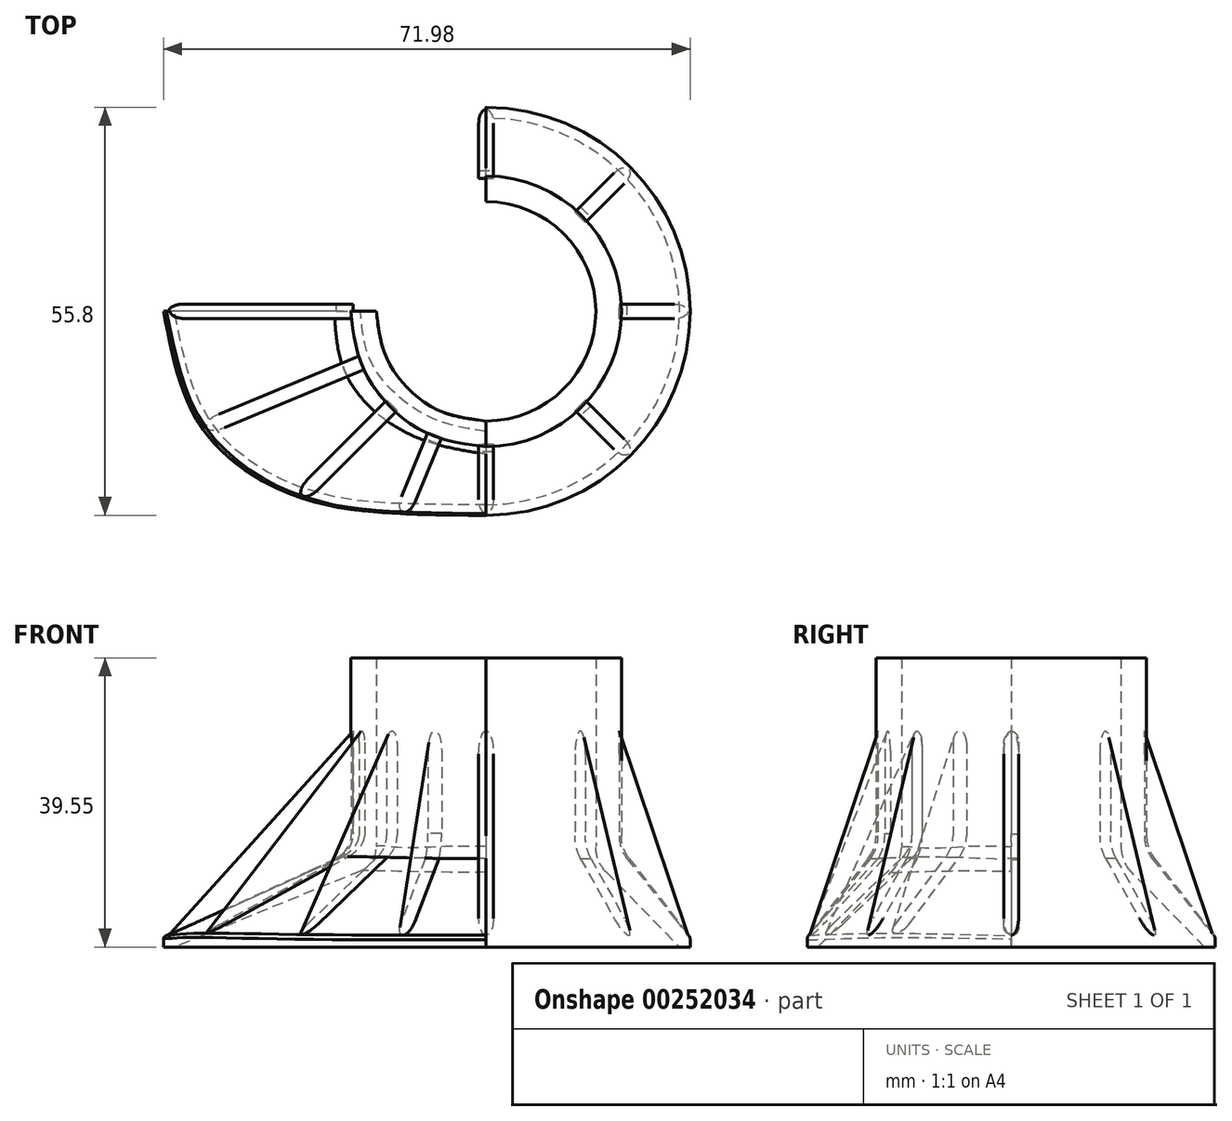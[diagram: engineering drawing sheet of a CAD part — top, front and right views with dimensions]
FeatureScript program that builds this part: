
annotation { "Feature Type Name" : "Feature", "Feature Type Description" : "" }
export const myFeature = defineFeature(function(context is Context, id is Id, definition is map)
    precondition{}
    {
        {
            var Q0;
            Q0=qCreatedBy(makeId("Front.planeOp"),FACE);
            var sketch = newSketch(context, id + "F0", { "sketchPlane" : qUnion([Q0])});
            skLineSegment(sketch, "E0.1", {"start": v(15, 34.55) * mm, "end": v(18.5, 34.55) * mm});
            skLineSegment(sketch, "E1", {"start": v(0, 0) * mm, "end": v(0, -5) * mm, "construction": true});
            skLineSegment(sketch, "E2", {"start": v(0, -5) * mm, "end": v(-50, -5) * mm, "construction": true});
            skLineSegment(sketch, "E3", {"start": v(0, -5) * mm, "end": v(27.9, -5) * mm, "construction": true});
            skLineSegment(sketch, "E4", {"start": v(0, 0) * mm, "end": v(0, 5) * mm, "construction": true});
            skLineSegment(sketch, "E5", {"start": v(0, 5) * mm, "end": v(-50, 5) * mm, "construction": true});
            skLineSegment(sketch, "E6", {"start": v(0, 5) * mm, "end": v(28.45, 5) * mm, "construction": true});
            skLineSegment(sketch, "E7", {"start": v(27.9, -5) * mm, "end": v(26.45, -5) * mm});
            skLineSegment(sketch, "E8", {"start": v(15, 34.55) * mm, "end": v(15, 8.73) * mm});
            skLineSegment(sketch, "E9", {"start": v(26.45, -5) * mm, "end": v(16.43, 5.23) * mm});
            skPoint(sketch, "E10.visualSharp", {"position": v(15, 6.7) * mm});
            skArc(sketch, "E10.filletArc", {"start": v(15, 8.73) * mm, "mid": v(15.37, 6.84) * mm, "end": v(16.43, 5.23) * mm});
            skLineSegment(sketch, "E11", {"start": v(18.5, 34.55) * mm, "end": v(18.5, 10.2) * mm});
            skLineSegment(sketch, "E12", {"start": v(19.55, 7.13) * mm, "end": v(27.7, -3.39) * mm});
            skLineSegment(sketch, "E13", {"start": v(27.9, -4) * mm, "end": v(27.9, -5) * mm});
            skPoint(sketch, "E14.visualSharp", {"position": v(27.9, -3.66) * mm});
            skArc(sketch, "E14.filletArc", {"start": v(27.9, -4) * mm, "mid": v(27.85, -3.68) * mm, "end": v(27.7, -3.39) * mm});
            skPoint(sketch, "E15.visualSharp", {"position": v(18.5, 8.48) * mm});
            skArc(sketch, "E15.filletArc", {"start": v(18.5, 10.2) * mm, "mid": v(18.77, 8.58) * mm, "end": v(19.55, 7.13) * mm});
            skLineSegment(sketch, "E16", {"start": v(0, 5) * mm, "end": v(0, 75) * mm, "construction": true});
            skLineSegment(sketch, "E17", {"start": v(0, -5) * mm, "end": v(0, -75) * mm, "construction": true});
            skSolve(sketch);
        }
        {
            var Q0;
            Q0=qCreatedBy(makeId("Front.planeOp"),FACE);
            var sketch = newSketch(context, id + "F1", { "sketchPlane" : qUnion([Q0])});
            skLineSegment(sketch, "E18.MirrorCS", {"start": v(-15, 34.55) * mm, "end": v(-15, 8.75) * mm});
            skLineSegment(sketch, "E19.MirrorCS", {"start": v(-15, 34.55) * mm, "end": v(-18.5, 34.55) * mm});
            skLineSegment(sketch, "E20.MirrorCS", {"start": v(-18.5, 34.55) * mm, "end": v(-18.5, 10.45) * mm});
            skLineSegment(sketch, "E21", {"start": v(-27.58, -5) * mm, "end": v(-42.58, -5) * mm, "construction": true});
            skLineSegment(sketch, "E22", {"start": v(-17.18, 5.4) * mm, "end": v(-42.58, -5) * mm});
            skLineSegment(sketch, "E23", {"start": v(-42.58, -5) * mm, "end": v(-44.08, -5) * mm});
            skLineSegment(sketch, "E24", {"start": v(-44.08, -5) * mm, "end": v(-44.08, -3.9) * mm});
            skLineSegment(sketch, "E25", {"start": v(-43.71, -3.44) * mm, "end": v(-20.75, 6.96) * mm});
            skPoint(sketch, "E26.visualSharp", {"position": v(-15, 6.28) * mm});
            skArc(sketch, "E26.filletArc", {"start": v(-17.18, 5.4) * mm, "mid": v(-15.6, 6.75) * mm, "end": v(-15, 8.75) * mm});
            skPoint(sketch, "E27.visualSharp", {"position": v(-18.5, 7.98) * mm});
            skArc(sketch, "E27.filletArc", {"start": v(-20.75, 6.96) * mm, "mid": v(-19.11, 8.38) * mm, "end": v(-18.5, 10.45) * mm});
            skPoint(sketch, "E28.visualSharp", {"position": v(-42.58, -5) * mm});
            skLineSegment(sketch, "E28.filletArc", {"start": v(-42.58, -5) * mm, "end": v(-42.58, -5) * mm});
            skPoint(sketch, "E29.visualSharp", {"position": v(-44.08, -3) * mm});
            skArc(sketch, "E29.filletArc", {"start": v(-43.71, -3.44) * mm, "mid": v(-43.97, -3.6) * mm, "end": v(-44.08, -3.9) * mm});
            skSolve(sketch);
        }
        {
            var Q0;
            Q0=makeQuery(id+"F0.imprint","IMPRINT",FACE,{"disambiguationData":[TD([[makeQuery(id+"F0.imprint","IMPRINT",EDGE,{"derivedFrom":sQuery(id+"F0.wireOp",EDGE,"E0.1")}),-1.0]])]});
            var Q1;
            Q1=sQuery(id+"F0.wireOp",EDGE,"E4");
            revolve(context, id + "F2", {"entities" : qUnion([Q0]), "axis" : qUnion([Q1]), "revolveType" : RevolveType.SYMMETRIC, "angle" : 180 * degree});
        }
        {
            var Q0;
            Q0=makeQuery(id+"F1.imprint","IMPRINT",FACE,{"disambiguationData":[TD([[makeQuery(id+"F1.imprint","IMPRINT",EDGE,{"derivedFrom":sQuery(id+"F1.wireOp",EDGE,"E18.MirrorCS")}),-1.0]])]});
            var Q1;
            Q1=sQuery(id+"F0.wireOp",EDGE,"E1");
            revolve(context, id + "F3", {"entities" : qUnion([Q0]), "axis" : qUnion([Q1]), "revolveType" : RevolveType.ONE_DIRECTION, "angle" : 45 * degree});
        }
        {
            var Q0;
            Q0=sQuery(id+"F0.wireOp",EDGE,"E16");
            cPlane(context, id + "F4", {"entities" : qUnion([Q0]), "cplaneType" : CPlaneType.LINE_ANGLE, "offset" : 25 * mm, "angle" : 45 * degree, "oppositeDirection" : true, "width" : 150 * mm, "height" : 150 * mm});
        }
        {
            var Q0;
            Q0=qCreatedBy(id+"F4.planeOp",FACE);
            var sketch = newSketch(context, id + "F5", { "sketchPlane" : qUnion([Q0])});
            skLineSegment(sketch, "E30.0", {"start": v(-35.71, -3.3) * mm, "end": v(-20.34, 7.3) * mm});
            skEllipticalArc(sketch, "E30.1", {});
            skEllipticalArc(sketch, "E30.2", {});
            skLineSegment(sketch, "E30.3", {"start": v(-16.68, 5.35) * mm, "end": v(-34.5, -5) * mm});
            skLineSegment(sketch, "E30.4", {"start": v(-36, -5) * mm, "end": v(-36, -3.94) * mm});
            skEllipticalArc(sketch, "E30.5", {});
            skLineSegment(sketch, "E30.7", {"start": v(-15, 34.55) * mm, "end": v(-15, 8.55) * mm});
            skLineSegment(sketch, "E30.8", {"start": v(-18.5, 34.55) * mm, "end": v(-18.5, 10.3) * mm});
            skLineSegment(sketch, "E31", {"start": v(-15, 34.55) * mm, "end": v(-18.5, 34.55) * mm});
            skLineSegment(sketch, "E32", {"start": v(-34.5, -5) * mm, "end": v(-36, -5) * mm});
            const initialGuessF5  = {"E30.1": [-0.026583616861920525, 0.010612693615257782, 0.06084566690226595, 0.9981471859496567, 0.004834134393264349, 0.00809347684792771, 4.060522833448642, 4.7487827347120035], "E30.2": [-0.017478025262984653, 0.009003997548478773, 0, 1, 0.0038585040043155883, 0.002495923514335722, 3.465495977855953, 4.59328952717254], "E30.5": [-0.035108957439661026, -0.00387137127108872, 0, 1, 0.0007819289924574948, 0.0008929977958457464, 0.7433772269077137, 1.6558872946807803]};
            skSetInitialGuess(sketch, initialGuessF5);
            skSolve(sketch);
        }
        {
            var Q0;
            Q0=sQuery(id+"F0.wireOp",EDGE,"E16");
            cPlane(context, id + "F6", {"entities" : qUnion([Q0]), "cplaneType" : CPlaneType.LINE_ANGLE, "offset" : 25 * mm, "angle" : 22.5 * degree, "oppositeDirection" : true, "width" : 150 * mm, "height" : 150 * mm});
        }
        {
            var Q0;
            Q0=qCreatedBy(id+"F6.planeOp",FACE);
            var sketch = newSketch(context, id + "F7", { "sketchPlane" : qUnion([Q0])});
            skLineSegment(sketch, "E33.0", {"start": v(-15, 34.55) * mm, "end": v(-15, 8.73) * mm});
            skLineSegment(sketch, "E33.1", {"start": v(-15, 34.55) * mm, "end": v(-18.5, 34.55) * mm});
            skLineSegment(sketch, "E33.2", {"start": v(-18.5, 34.55) * mm, "end": v(-18.5, 10.56) * mm});
            skEllipticalArc(sketch, "E33.3", {});
            skEllipticalArc(sketch, "E33.4", {});
            skLineSegment(sketch, "E33.5", {"start": v(-28.48, -5) * mm, "end": v(-16.32, 5.23) * mm});
            skLineSegment(sketch, "E33.6", {"start": v(-19.47, 7.14) * mm, "end": v(-29.7, -3.38) * mm});
            skLineSegment(sketch, "E33.7", {"start": v(-29.97, -5) * mm, "end": v(-28.48, -5) * mm});
            skLineSegment(sketch, "E33.8", {"start": v(-29.97, -4.01) * mm, "end": v(-29.97, -5) * mm});
            skEllipticalArc(sketch, "E33.9", {});
            const initialGuessF7  = {"E33.3": [-0.022046031430363655, 0.01037504244595766, 0, 1, 0.0047150366026541, 0.003548654282312673, 3.9552031679487514, 4.7508680209378245], "E33.4": [-0.019619401620108803, 0.00873068936393129, 0, 1, 0.005, 0.00461939766255638, 3.937421198959029, 4.71238898038469], "E33.9": [-0.029358914034073286, -0.003991737384349152, 0, 1, 0.0007292771105017406, 0.0006075253392299736, 0.582676780905518, 1.5997427680559044]};
            skSetInitialGuess(sketch, initialGuessF7);
            skSolve(sketch);
        }
        {
            var Q0;
            Q0=sQuery(id+"F0.wireOp",EDGE,"E16");
            cPlane(context, id + "F8", {"entities" : qUnion([Q0]), "cplaneType" : CPlaneType.LINE_ANGLE, "offset" : 25 * mm, "angle" : 67.5 * degree, "oppositeDirection" : true, "width" : 150 * mm, "height" : 150 * mm});
        }
        {
            var Q0;
            Q0=qCreatedBy(id+"F8.planeOp",FACE);
            var sketch = newSketch(context, id + "F9", { "sketchPlane" : qUnion([Q0])});
            skLineSegment(sketch, "E34.0", {"start": v(-15, 34.55) * mm, "end": v(-15, 8.79) * mm});
            skLineSegment(sketch, "E34.2", {"start": v(-18.5, 34.55) * mm, "end": v(-18.5, 10.22) * mm});
            skEllipticalArc(sketch, "E34.3", {});
            skEllipticalArc(sketch, "E34.4", {});
            skLineSegment(sketch, "E34.5", {"start": v(-17.17, 5.43) * mm, "end": v(-40.48, -5) * mm});
            skLineSegment(sketch, "E34.6", {"start": v(-41.48, -3.12) * mm, "end": v(-21, 7.3) * mm});
            skLineSegment(sketch, "E34.8", {"start": v(-41.98, -5) * mm, "end": v(-41.93, -3.7) * mm});
            skEllipticalArc(sketch, "E34.9", {});
            skLineSegment(sketch, "E35", {"start": v(-15, 34.55) * mm, "end": v(-18.5, 34.55) * mm});
            skLineSegment(sketch, "E36", {"start": v(-40.48, -5) * mm, "end": v(-41.98, -5) * mm});
            const initialGuessF9  = {"E34.3": [-0.04614806816616966, 0.007846815310961371, -0.09026721845856622, 0.9959175815662383, 0.006463787194736521, 0.027755268022550284, 4.263265283072879, 4.691284056141345], "E34.4": [-0.01866540415463741, 0.008792156648103917, -0.0707566274833398, 0.9974936088352573, 0.0036803664035136535, 0.003664902615111489, 3.490244967548646, 4.641275381153363], "E34.9": [-0.040591018842124155, -0.003937842435516913, 0, 1, 0.0010684791335107172, 0.0013767747960735449, 0.7037044416214746, 1.346265545729727]};
            skSetInitialGuess(sketch, initialGuessF9);
            skSolve(sketch);
        }
        {
            var Q1;
            Q1=makeQuery(id+"F2.opRevolve","CAP_FACE",FACE,{"disambiguationData":[OSD([sQuery(id+"F0.wireOp",EDGE,"E0.1"),sQuery(id+"F0.wireOp",EDGE,"E7"),sQuery(id+"F0.wireOp",EDGE,"E8"),sQuery(id+"F0.wireOp",EDGE,"E9"),sQuery(id+"F0.wireOp",EDGE,"E10.filletArc"),sQuery(id+"F0.wireOp",EDGE,"E11"),sQuery(id+"F0.wireOp",EDGE,"E12"),sQuery(id+"F0.wireOp",EDGE,"E13"),sQuery(id+"F0.wireOp",EDGE,"E14.filletArc"),sQuery(id+"F0.wireOp",EDGE,"E15.filletArc")])],"isStart":true});
            var Q2;
            Q2=makeQuery(id+"F7.imprint","IMPRINT",FACE,{"disambiguationData":[TD([[makeQuery(id+"F7.imprint","IMPRINT",EDGE,{"derivedFrom":sQuery(id+"F7.wireOp",EDGE,"E33.0")}),-1.0]])]});
            var Q3;
            Q3=makeQuery(id+"F5.imprint","IMPRINT",FACE,{"disambiguationData":[TD([[makeQuery(id+"F5.imprint","IMPRINT",EDGE,{"derivedFrom":sQuery(id+"F5.wireOp",EDGE,"E30.0")}),-1.0]])]});
            var Q4;
            Q4=makeQuery(id+"F9.imprint","IMPRINT",FACE,{"disambiguationData":[TD([[makeQuery(id+"F9.imprint","IMPRINT",EDGE,{"derivedFrom":sQuery(id+"F9.wireOp",EDGE,"E34.0")}),-1.0]])]});
            var Q5;
            Q5=makeQuery(id+"F1.imprint","IMPRINT",FACE,{"disambiguationData":[TD([[makeQuery(id+"F1.imprint","IMPRINT",EDGE,{"derivedFrom":sQuery(id+"F1.wireOp",EDGE,"E18.MirrorCS")}),-1.0]])]});
            loft(context, id + "F10", {"sheetProfilesArray" : [{ "sheetProfileEntities" : qUnion([Q1]) }, { "sheetProfileEntities" : qUnion([Q2]) }, { "sheetProfileEntities" : qUnion([Q3]) }, { "sheetProfileEntities" : qUnion([Q4]) }, { "sheetProfileEntities" : qUnion([Q5]) }]});
        }
        {
            var Q0;
            Q0=qCreatedBy(makeId("Front.planeOp"),FACE);
            var sketch = newSketch(context, id + "F11", { "sketchPlane" : qUnion([Q0])});
            skLineSegment(sketch, "E37.0", {"start": v(-18.2, 10.45) * mm, "end": v(-18.2, 24.55) * mm});
            skFitSpline(sketch, "E37.1", {"points": [v(-20.45, 6.96) * mm, v(-20.28, 7.04) * mm, v(-20.12, 7.12) * mm, v(-19.97, 7.22) * mm, v(-19.82, 7.32) * mm, v(-19.67, 7.43) * mm, v(-19.53, 7.55) * mm, v(-19.4, 7.67) * mm, v(-19.26, 7.8) * mm, v(-19.14, 7.94) * mm, v(-19.02, 8.07) * mm, v(-18.91, 8.22) * mm, v(-18.81, 8.38) * mm, v(-18.71, 8.53) * mm, v(-18.62, 8.69) * mm, v(-18.55, 8.86) * mm, v(-18.47, 9.02) * mm, v(-18.4, 9.2) * mm, v(-18.36, 9.37) * mm, v(-18.3, 9.55) * mm, v(-18.27, 9.72) * mm, v(-18.24, 9.9) * mm, v(-18.21, 10.09) * mm, v(-18.2, 10.27) * mm, v(-18.2, 10.45) * mm]});
            skLineSegment(sketch, "E37.2", {"start": v(-43.41, -3.44) * mm, "end": v(-20.45, 6.96) * mm});
            skLineSegment(sketch, "E38", {"start": v(-18.2, 24.55) * mm, "end": v(-43.41, -3.44) * mm});
            skPoint(sketch, "E39.orphan", {"position": v(-18.5, 34.55) * mm});
            skSolve(sketch);
        }
        {
            var Q0;
            Q0=qCreatedBy(id+"F8.planeOp",FACE);
            var sketch = newSketch(context, id + "F12", { "sketchPlane" : qUnion([Q0])});
            skLineSegment(sketch, "E40.0", {"start": v(-18.4, 24.55) * mm, "end": v(-18.4, 10.22) * mm});
            skEllipticalArc(sketch, "E40.1", {});
            skLineSegment(sketch, "E40.2", {"start": v(-41.38, -3.12) * mm, "end": v(-20.9, 7.3) * mm});
            skLineSegment(sketch, "E41", {"start": v(-18.4, 24.55) * mm, "end": v(-41.38, -3.12) * mm});
            const initialGuessF12  = {"E40.1": [-0.04604806816616966, 0.007846815310961371, -0.9959175815657446, -0.09026721845852147, 0.027755268022550284, 0.006463787194736521, 2.692468956277983, 3.120487729346449]};
            skSetInitialGuess(sketch, initialGuessF12);
            skSolve(sketch);
        }
        {
            var Q0;
            Q0=qCreatedBy(id+"F4.planeOp",FACE);
            var sketch = newSketch(context, id + "F13", { "sketchPlane" : qUnion([Q0])});
            skLineSegment(sketch, "E42.0", {"start": v(-18.2, 24.55) * mm, "end": v(-18.2, 10.3) * mm});
            skEllipticalArc(sketch, "E42.1", {});
            skLineSegment(sketch, "E42.2", {"start": v(-35.61, -3.3) * mm, "end": v(-20.04, 7.3) * mm});
            skLineSegment(sketch, "E43", {"start": v(-18.2, 24.55) * mm, "end": v(-35.61, -3.3) * mm});
            const initialGuessF13  = {"E42.1": [-0.026283616861920527, 0.010612693615257782, -0.9981471859496567, 0.060845666902265956, 0.00809347684792771, 0.004834134393264349, 2.4897265066537453, 3.1779864079171056]};
            skSetInitialGuess(sketch, initialGuessF13);
            skSolve(sketch);
        }
        {
            var Q0;
            Q0=qCreatedBy(id+"F6.planeOp",FACE);
            var sketch = newSketch(context, id + "F14", { "sketchPlane" : qUnion([Q0])});
            skLineSegment(sketch, "E44.0", {"start": v(-19.27, 7.14) * mm, "end": v(-29.7, -3.38) * mm});
            skEllipticalArc(sketch, "E44.1", {});
            skLineSegment(sketch, "E44.2", {"start": v(-18.3, 24.55) * mm, "end": v(-18.3, 10.56) * mm});
            skLineSegment(sketch, "E45", {"start": v(-18.3, 24.55) * mm, "end": v(-29.7, -3.38) * mm});
            const initialGuessF14  = {"E44.1": [-0.021846031430363656, 0.01037504244595766, 0, 1, 0.0047150366026541, 0.003548654282312673, 3.955203167948752, 4.7508680209378245]};
            skSetInitialGuess(sketch, initialGuessF14);
            skSolve(sketch);
        }
        {
            var Q0;
            Q0=qCreatedBy(makeId("Right.planeOp"),FACE);
            var sketch = newSketch(context, id + "F15", { "sketchPlane" : qUnion([Q0])});
            skLineSegment(sketch, "E46.0", {"start": v(-19.25, 7.13) * mm, "end": v(-27.6, -3.39) * mm});
            skArc(sketch, "E46.1", {"start": v(-18.2, 10.2) * mm, "mid": v(-18.47, 8.58) * mm, "end": v(-19.25, 7.13) * mm});
            skLineSegment(sketch, "E46.2", {"start": v(-18.2, 24.55) * mm, "end": v(-18.2, 10.2) * mm});
            skLineSegment(sketch, "E47", {"start": v(-18.2, 24.55) * mm, "end": v(-27.6, -3.39) * mm});
            skSolve(sketch);
        }
        {
            var Q0;
            Q0=makeQuery(id+"F3.opRevolve","SWEPT_BODY",BODY,{"disambiguationData":[OSD([sQuery(id+"F1.wireOp",EDGE,"E18.MirrorCS"),sQuery(id+"F1.wireOp",EDGE,"E19.MirrorCS"),sQuery(id+"F1.wireOp",EDGE,"E20.MirrorCS"),sQuery(id+"F1.wireOp",EDGE,"E22"),sQuery(id+"F1.wireOp",EDGE,"E23"),sQuery(id+"F1.wireOp",EDGE,"E24"),sQuery(id+"F1.wireOp",EDGE,"E25"),sQuery(id+"F1.wireOp",EDGE,"E26.filletArc"),sQuery(id+"F1.wireOp",EDGE,"E27.filletArc"),sQuery(id+"F1.wireOp",EDGE,"E29.filletArc")])]});
            deleteBodies(context, id + "F16", {"entities" : qUnion([Q0])});
        }
        {
            var Q0;
            Q0=makeQuery(id+"F14.imprint","IMPRINT",FACE,{"disambiguationData":[TD([[makeQuery(id+"F14.imprint","IMPRINT",EDGE,{"derivedFrom":sQuery(id+"F14.wireOp",EDGE,"E44.0")}),-1.0]])]});
            extrude(context, id + "F17", {"entities" : qUnion([Q0]), "endBound" : BoundingType.SYMMETRIC, "depth" : 2 * mm});
        }
        {
            var Q0;
            Q0=makeQuery(id+"F13.imprint","IMPRINT",FACE,{"disambiguationData":[TD([[makeQuery(id+"F13.imprint","IMPRINT",EDGE,{"derivedFrom":sQuery(id+"F13.wireOp",EDGE,"E42.0")}),-1.0]])]});
            extrude(context, id + "F18", {"entities" : qUnion([Q0]), "endBound" : BoundingType.SYMMETRIC, "depth" : 2 * mm});
        }
        {
            var Q0;
            Q0=makeQuery(id+"F12.imprint","IMPRINT",FACE,{"disambiguationData":[TD([[makeQuery(id+"F12.imprint","IMPRINT",EDGE,{"derivedFrom":sQuery(id+"F12.wireOp",EDGE,"E40.0")}),-1.0]])]});
            extrude(context, id + "F19", {"entities" : qUnion([Q0]), "endBound" : BoundingType.SYMMETRIC, "depth" : 2 * mm});
        }
        {
            var Q0;
            Q0=makeQuery(id+"F11.imprint","IMPRINT",FACE,{"disambiguationData":[TD([[makeQuery(id+"F11.imprint","IMPRINT",EDGE,{"derivedFrom":sQuery(id+"F11.wireOp",EDGE,"E37.0")}),1.0]])]});
            extrude(context, id + "F20", {"entities" : qUnion([Q0]), "depth" : 1 * mm});
        }
        {
            var Q0;
            Q0=makeQuery(id+"F20.opExtrude","CAP_EDGE",EDGE,{"disambiguationData":[OSD([sQuery(id+"F11.wireOp",EDGE,"E38")])],"isStart":false});
            var Q1;
            Q1=makeQuery(id+"F19.opExtrude","CAP_EDGE",EDGE,{"disambiguationData":[OSD([sQuery(id+"F12.wireOp",EDGE,"E41")])],"isStart":false});
            var Q2;
            Q2=makeQuery(id+"F19.opExtrude","CAP_EDGE",EDGE,{"disambiguationData":[OSD([sQuery(id+"F12.wireOp",EDGE,"E41")])],"isStart":true});
            var Q3;
            Q3=makeQuery(id+"F18.opExtrude","CAP_EDGE",EDGE,{"disambiguationData":[OSD([sQuery(id+"F13.wireOp",EDGE,"E43")])],"isStart":false});
            var Q4;
            Q4=makeQuery(id+"F18.opExtrude","CAP_EDGE",EDGE,{"disambiguationData":[OSD([sQuery(id+"F13.wireOp",EDGE,"E43")])],"isStart":true});
            var Q5;
            Q5=makeQuery(id+"F17.opExtrude","CAP_EDGE",EDGE,{"disambiguationData":[OSD([sQuery(id+"F14.wireOp",EDGE,"E45")])],"isStart":true});
            var Q6;
            Q6=makeQuery(id+"F17.opExtrude","CAP_EDGE",EDGE,{"disambiguationData":[OSD([sQuery(id+"F14.wireOp",EDGE,"E45")])],"isStart":false});
            fillet(context, id + "F21", {"entities" : qUnion([Q0, Q1, Q2, Q3, Q4, Q5, Q6]), "radius" : 1 * mm, "tangentPropagation" : true, "allowEdgeOverflow" : false});
        }
        {
            var Q0;
            Q0=makeQuery(id+"F20.opExtrude","SWEPT_BODY",BODY,{"disambiguationData":[OSD([sQuery(id+"F11.wireOp",EDGE,"E37.0"),sQuery(id+"F11.wireOp",EDGE,"E37.1"),sQuery(id+"F11.wireOp",EDGE,"E37.2"),sQuery(id+"F11.wireOp",EDGE,"E38")])]});
            var Q1;
            Q1=qCreatedBy(makeId("Front.planeOp"),FACE);
            mirror(context, id + "F22", {"operationType" : NewBodyOperationType.ADD, "entities" : qUnion([Q0]), "mirrorPlane" : qUnion([Q1])});
        }
        {
            var Q0;
            Q0=makeQuery(id+"F15.imprint","IMPRINT",FACE,{"disambiguationData":[TD([[makeQuery(id+"F15.imprint","IMPRINT",EDGE,{"derivedFrom":sQuery(id+"F15.wireOp",EDGE,"E46.0")}),-1.0]])]});
            extrude(context, id + "F23", {"entities" : qUnion([Q0]), "endBound" : BoundingType.SYMMETRIC, "depth" : 2 * mm});
        }
        {
            var Q0;
            Q0=makeQuery(id+"F23.opExtrude","CAP_EDGE",EDGE,{"disambiguationData":[OSD([sQuery(id+"F15.wireOp",EDGE,"E47")])],"isStart":true});
            var Q1;
            Q1=makeQuery(id+"F23.opExtrude","CAP_EDGE",EDGE,{"disambiguationData":[OSD([sQuery(id+"F15.wireOp",EDGE,"E47")])],"isStart":false});
            fillet(context, id + "F24", {"entities" : qUnion([Q0, Q1]), "radius" : 1 * mm, "tangentPropagation" : true, "allowEdgeOverflow" : false});
        }
        {
            var Q0;
            Q0=makeQuery(id+"F23.opExtrude","SWEPT_BODY",BODY,{"disambiguationData":[OSD([sQuery(id+"F15.wireOp",EDGE,"E46.0"),sQuery(id+"F15.wireOp",EDGE,"E46.1"),sQuery(id+"F15.wireOp",EDGE,"E46.2"),sQuery(id+"F15.wireOp",EDGE,"E47")])]});
            var Q1;
            Q1=sQuery(id+"F0.wireOp",EDGE,"E16");
            circularPattern(context, id + "F25", {"entities" : qUnion([Q0]), "axis" : qUnion([Q1]), "angle" : 180 * degree, "instanceCount" : 5, "equalSpace" : true});
        }
    });
